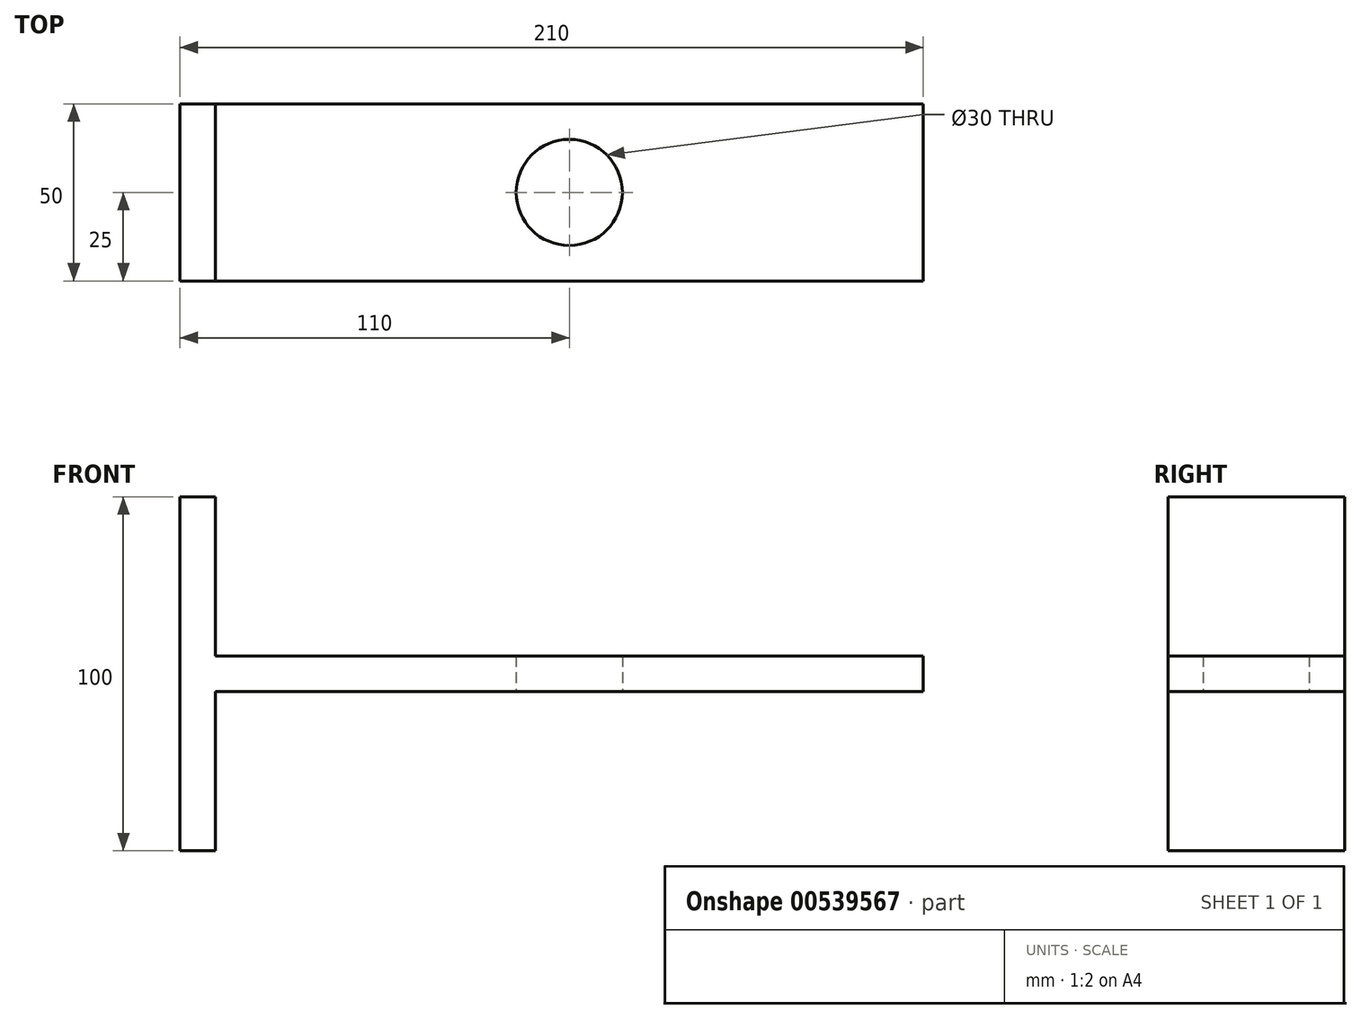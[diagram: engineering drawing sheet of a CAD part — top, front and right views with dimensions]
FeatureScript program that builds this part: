
annotation { "Feature Type Name" : "Feature", "Feature Type Description" : "" }
export const myFeature = defineFeature(function(context is Context, id is Id, definition is map)
    precondition{}
    {
        {
            var Q0;
            Q0=qCreatedBy(makeId("Top.planeOp"),FACE);
            var sketch = newSketch(context, id + "F0", { "sketchPlane" : qUnion([Q0])});
            skLineSegment(sketch, "E0.bottom", {"start": v(-100, 25) * mm, "end": v(100, 25) * mm});
            skLineSegment(sketch, "E0.top", {"start": v(-100, -25) * mm, "end": v(100, -25) * mm});
            skLineSegment(sketch, "E0.left", {"start": v(-100, 25) * mm, "end": v(-100, -25) * mm});
            skLineSegment(sketch, "E0.right", {"start": v(100, 25) * mm, "end": v(100, -25) * mm});
            skPoint(sketch, "E0.middle", {"position": v(0, 0) * mm});
            skCircle(sketch, "E1", {"center": v(0, 0) * mm, "radius": 15 * mm});
            skSolve(sketch);
        }
        {
            var Q0;
            Q0 = qSketchRegion(id + "F0", true);
            extrude(context, id + "F1", {"entities" : qUnion([Q0]), "endBound" : BoundingType.SYMMETRIC, "depth" : 10 * mm, "offsetDistance" : 25 * mm});
        }
        {
            var Q0;
            Q0=makeQuery(id+"F1.opExtrude","SWEPT_FACE",FACE,{"disambiguationData":[OSD([sQuery(id+"F0.wireOp",EDGE,"E0.left")])]});
            var sketch = newSketch(context, id + "F2", { "sketchPlane" : qUnion([Q0])});
            skLineSegment(sketch, "E2.bottom", {"start": v(-25, 50) * mm, "end": v(25, 50) * mm});
            skLineSegment(sketch, "E2.top", {"start": v(-25, -50) * mm, "end": v(25, -50) * mm});
            skLineSegment(sketch, "E2.left", {"start": v(-25, 50) * mm, "end": v(-25, -50) * mm});
            skLineSegment(sketch, "E2.right", {"start": v(25, 50) * mm, "end": v(25, -50) * mm});
            skPoint(sketch, "E2.middle", {"position": v(0, 0) * mm});
            skSolve(sketch);
        }
        {
            var Q0;
            Q0 = qSketchRegion(id + "F2", true);
            extrude(context, id + "F3", {"entities" : qUnion([Q0]), "operationType" : NewBodyOperationType.ADD, "depth" : 10 * mm, "offsetDistance" : 25 * mm});
        }
    });
